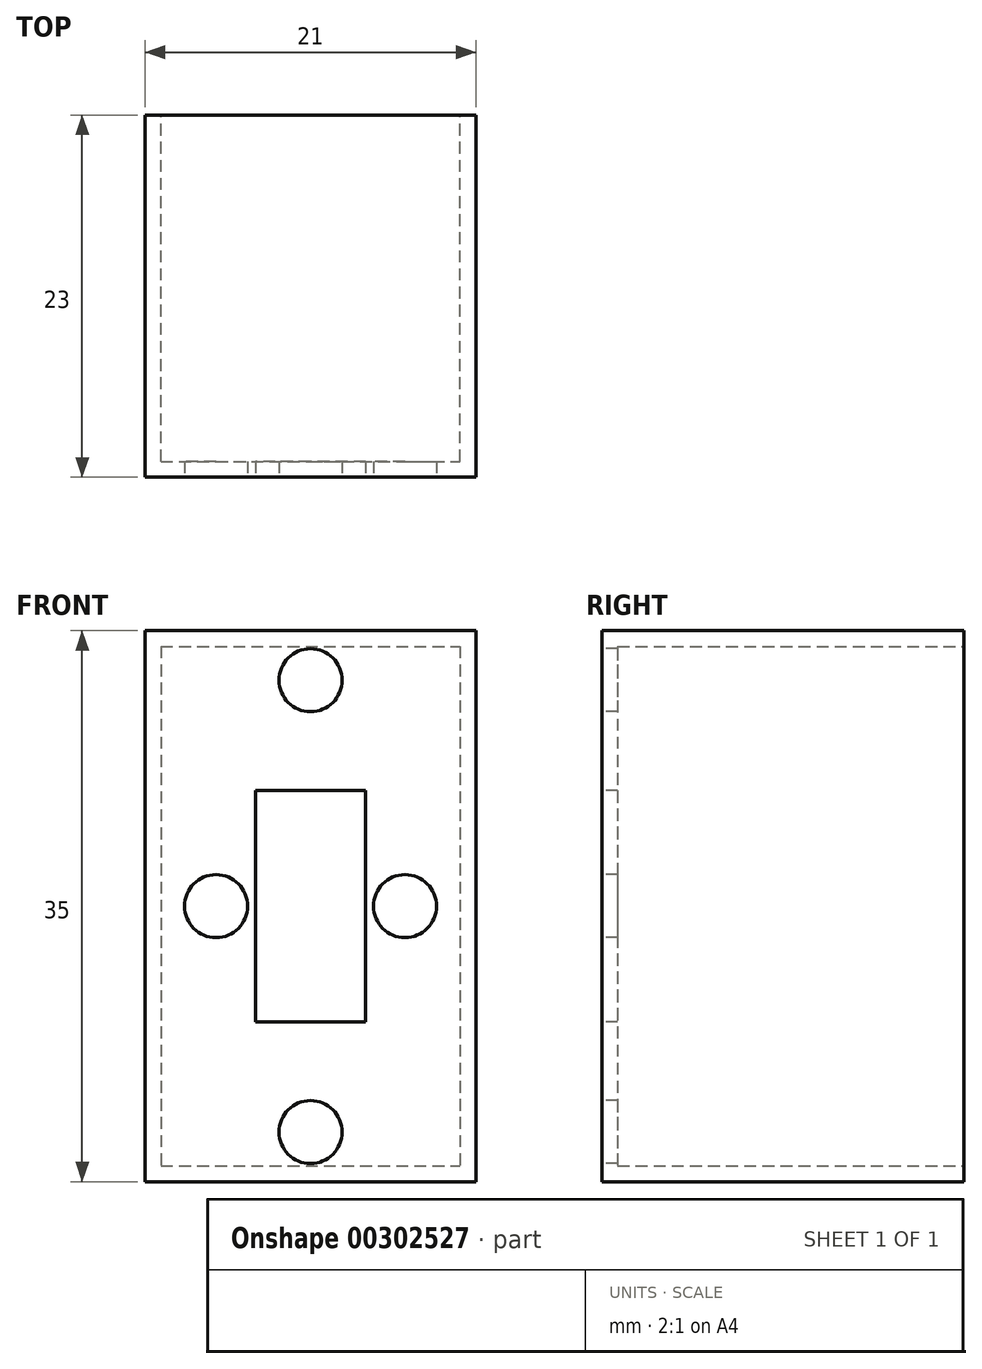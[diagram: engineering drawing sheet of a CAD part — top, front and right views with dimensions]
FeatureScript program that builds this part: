
annotation { "Feature Type Name" : "Feature", "Feature Type Description" : "" }
export const myFeature = defineFeature(function(context is Context, id is Id, definition is map)
    precondition{}
    {
        {
            assignVariable(context, id + "F0", {"name" : "depth", "anyValue" : 22});
        }
        {
            var Q0;
            Q0=qCreatedBy(makeId("Front.planeOp"),FACE);
            var sketch = newSketch(context, id + "F1", { "sketchPlane" : qUnion([Q0])});
            skLineSegment(sketch, "E0.bottom", {"start": v(-10.5, 17.5) * mm, "end": v(10.5, 17.5) * mm});
            skLineSegment(sketch, "E0.top", {"start": v(-10.5, -17.5) * mm, "end": v(10.5, -17.5) * mm});
            skLineSegment(sketch, "E0.left", {"start": v(-10.5, 17.5) * mm, "end": v(-10.5, -17.5) * mm});
            skLineSegment(sketch, "E0.right", {"start": v(10.5, 17.5) * mm, "end": v(10.5, -17.5) * mm});
            skPoint(sketch, "E0.middle", {"position": v(0, 0) * mm});
            skSolve(sketch);
        }
        {
            var Q0;
            Q0=makeQuery(id+"F1.imprint","IMPRINT",FACE,{"disambiguationData":[TD([[makeQuery(id+"F1.imprint","IMPRINT",EDGE,{"derivedFrom":sQuery(id+"F1.wireOp",EDGE,"E0.bottom")}),-1.0]])]});
            extrude(context, id + "F2", {"entities" : qUnion([Q0]), "oppositeDirection" : true, "depth" : (getVariable(context, 'depth') + 1) * mm});
        }
        {
            var Q0;
            Q0=makeQuery(id+"F2.opExtrude","CAP_FACE",FACE,{"disambiguationData":[OSD([sQuery(id+"F1.wireOp",EDGE,"E0.bottom"),sQuery(id+"F1.wireOp",EDGE,"E0.top"),sQuery(id+"F1.wireOp",EDGE,"E0.left"),sQuery(id+"F1.wireOp",EDGE,"E0.right")])],"isStart":false});
            var sketch = newSketch(context, id + "F3", { "sketchPlane" : qUnion([Q0])});
            skLineSegment(sketch, "E1.bottom", {"start": v(9.5, 16.5) * mm, "end": v(-9.5, 16.5) * mm});
            skLineSegment(sketch, "E1.top", {"start": v(9.5, -16.5) * mm, "end": v(-9.5, -16.5) * mm});
            skLineSegment(sketch, "E1.left", {"start": v(9.5, 16.5) * mm, "end": v(9.5, -16.5) * mm});
            skLineSegment(sketch, "E1.right", {"start": v(-9.5, 16.5) * mm, "end": v(-9.5, -16.5) * mm});
            skPoint(sketch, "E1.middle", {"position": v(0, 0) * mm});
            skSolve(sketch);
        }
        {
            var Q0;
            Q0=makeQuery(id+"F3.imprint","IMPRINT",FACE,{"disambiguationData":[TD([[makeQuery(id+"F3.imprint","IMPRINT",EDGE,{"derivedFrom":sQuery(id+"F3.wireOp",EDGE,"E1.bottom")}),1.0]])]});
            extrude(context, id + "F4", {"entities" : qUnion([Q0]), "operationType" : NewBodyOperationType.REMOVE, "oppositeDirection" : true, "depth" : (getVariable(context, 'depth')) * mm});
        }
        {
            var Q0;
            Q0=qCreatedBy(makeId("Front.planeOp"),FACE);
            var sketch = newSketch(context, id + "F5", { "sketchPlane" : qUnion([Q0])});
            skLineSegment(sketch, "E2.bottom", {"start": v(-3.5, -7.35) * mm, "end": v(3.5, -7.35) * mm});
            skLineSegment(sketch, "E2.top", {"start": v(-3.5, 7.35) * mm, "end": v(3.5, 7.35) * mm});
            skLineSegment(sketch, "E2.left", {"start": v(-3.5, -7.35) * mm, "end": v(-3.5, 7.35) * mm});
            skLineSegment(sketch, "E2.right", {"start": v(3.5, -7.35) * mm, "end": v(3.5, 7.35) * mm});
            skPoint(sketch, "E2.middle", {"position": v(0, 0) * mm});
            skSolve(sketch);
        }
        {
            var Q0;
            Q0=makeQuery(id+"F5.imprint","IMPRINT",FACE,{"disambiguationData":[TD([[makeQuery(id+"F5.imprint","IMPRINT",EDGE,{"derivedFrom":sQuery(id+"F5.wireOp",EDGE,"E2.bottom")}),1.0]])]});
            extrude(context, id + "F6", {"entities" : qUnion([Q0]), "operationType" : NewBodyOperationType.REMOVE, "oppositeDirection" : true, "depth" : 25 * mm});
        }
        {
            var Q0;
            Q0=makeQuery(id+"F2.opExtrude","CAP_FACE",FACE,{"disambiguationData":[OSD([sQuery(id+"F1.wireOp",EDGE,"E0.bottom"),sQuery(id+"F1.wireOp",EDGE,"E0.top"),sQuery(id+"F1.wireOp",EDGE,"E0.left"),sQuery(id+"F1.wireOp",EDGE,"E0.right")])],"isStart":true});
            var sketch = newSketch(context, id + "F7", { "sketchPlane" : qUnion([Q0])});
            skPoint(sketch, "E3", {"position": v(0, 7.35) * mm});
            skPoint(sketch, "E4", {"position": v(0, 14.35) * mm});
            skPoint(sketch, "E5", {"position": v(0, -7.35) * mm});
            skPoint(sketch, "E6", {"position": v(0, -14.35) * mm});
            skPoint(sketch, "E7", {"position": v(-6, 0) * mm});
            skPoint(sketch, "E7.positionSnap0", {"position": v(-3.5, 0) * mm});
            skPoint(sketch, "E8", {"position": v(6, 0) * mm});
            skPoint(sketch, "E8.positionSnap0", {"position": v(3.5, 0) * mm});
            skSolve(sketch);
        }
        {
            var Q0;
            Q0=sQuery(id+"F7.wireOp",VERTEX,"E4");
            var Q1;
            Q1=sQuery(id+"F7.wireOp",VERTEX,"E7");
            var Q2;
            Q2=sQuery(id+"F7.wireOp",VERTEX,"E8");
            var Q3;
            Q3=sQuery(id+"F7.wireOp",VERTEX,"E6");
            var Q4;
            Q4=makeQuery(id+"F2.opExtrude","SWEPT_BODY",BODY,{"disambiguationData":[OSD([sQuery(id+"F1.wireOp",EDGE,"E0.bottom"),sQuery(id+"F1.wireOp",EDGE,"E0.top"),sQuery(id+"F1.wireOp",EDGE,"E0.left"),sQuery(id+"F1.wireOp",EDGE,"E0.right")])]});
            hole(context, id + "F8", {"style" : HoleStyle.SIMPLE, "endStyle" : HoleEndStyle.BLIND, "holeDiameter" : 4 * mm, "holeDepth" : 6 * mm, "isTappedThrough" : true, "tappedDepth" : 12 * mm, "tapClearance" : 3, "locations" : qUnion([Q0, Q1, Q2, Q3]), "scope" : qUnion([Q4])});
        }
    });
